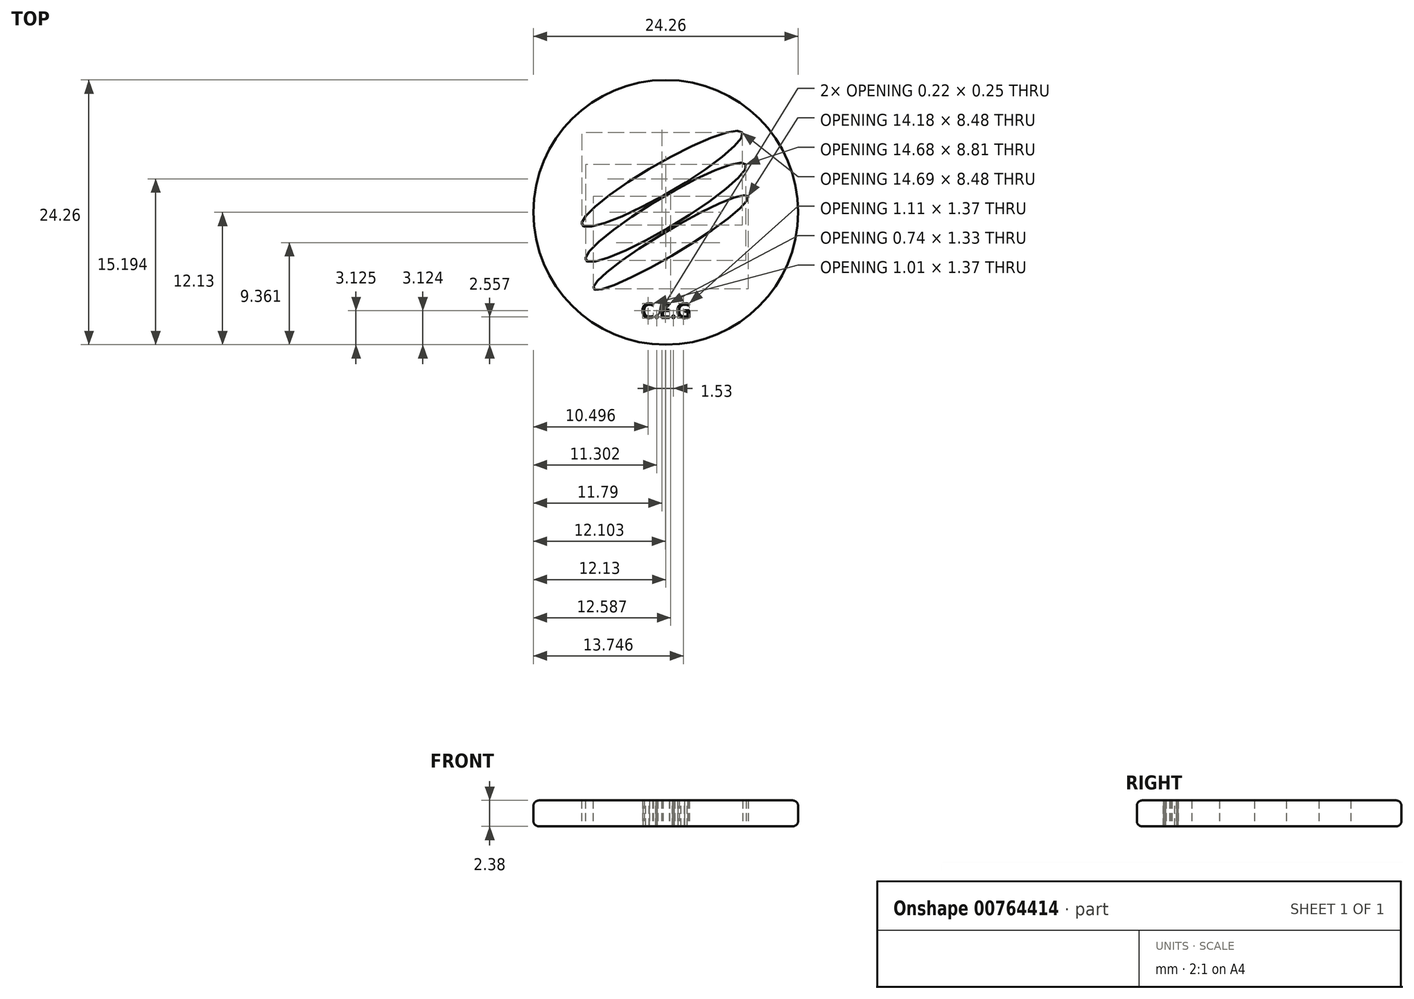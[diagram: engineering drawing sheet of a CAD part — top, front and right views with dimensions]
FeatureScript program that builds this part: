
annotation { "Feature Type Name" : "Feature", "Feature Type Description" : "" }
export const myFeature = defineFeature(function(context is Context, id is Id, definition is map)
    precondition{}
    {
        {
            assignVariable(context, id + "F0", {"name" : "Spessore", "anyValue" : 2.38});
        }
        {
            var Q0;
            Q0=qCreatedBy(makeId("Top.planeOp"),FACE);
            var sketch = newSketch(context, id + "F1", { "sketchPlane" : qUnion([Q0])});
            skCircle(sketch, "E0", {"center": v(0, 0) * mm, "radius": 12.12 * mm});
            skEllipse(sketch, "E1", {"center": v(-0.34, 3.06) * mm, "majorRadius": 8.48 * mm, "minorRadius": 1.38 * mm, "majorAxis": v(0.87, 0.5)});
            skEllipse(sketch, "E2", {"center": v(0, 0) * mm, "majorRadius": 8.56 * mm, "minorRadius": 1.35 * mm, "majorAxis": v(0.86, 0.51)});
            skEllipse(sketch, "E3", {"center": v(0.46, -2.77) * mm, "majorRadius": 8.26 * mm, "minorRadius": 1.08 * mm, "majorAxis": v(0.86, 0.51)});
            skText(sketch, "E4", { "text": "C.E.G", "fontName": "OpenSans-Regular.ttf"});
            const initialGuessF1  = {"E4": [-0.00225, -0.00967, 1, 0, 0.00134]};
            skSetInitialGuess(sketch, initialGuessF1);
            skSolve(sketch);
        }
        {
            var Q0;
            Q0=makeQuery(id+"F1.imprint","IMPRINT",FACE,{"disambiguationData":[TD([[makeQuery(id+"F1.imprint","IMPRINT",EDGE,{"derivedFrom":sQuery(id+"F1.wireOp",EDGE,"E0")}),1.0]])]});
            extrude(context, id + "F2", {"entities" : qUnion([Q0]), "depth" : (getVariable(context, 'Spessore')) * mm, "offsetDistance" : 25 * mm});
        }
        {
            var Q0;
            Q0=makeQuery(id+"F2.opExtrude","CAP_EDGE",EDGE,{"disambiguationData":[OSD([sQuery(id+"F1.wireOp",EDGE,"E0")])],"isStart":false});
            var Q1;
            Q1=makeQuery(id+"F2.opExtrude","CAP_EDGE",EDGE,{"disambiguationData":[OSD([sQuery(id+"F1.wireOp",EDGE,"E0")])],"isStart":true});
            fillet(context, id + "F3", {"entities" : qUnion([Q0, Q1]), "radius" : .5 * mm, "tangentPropagation" : true, "allowEdgeOverflow" : false});
        }
    });
